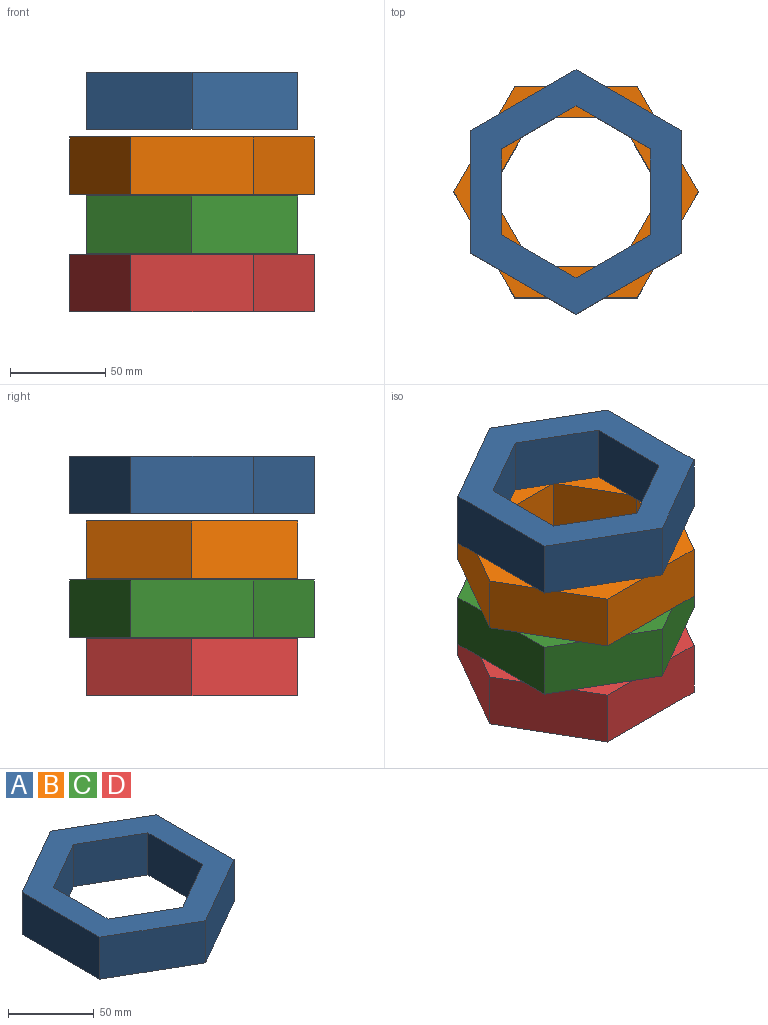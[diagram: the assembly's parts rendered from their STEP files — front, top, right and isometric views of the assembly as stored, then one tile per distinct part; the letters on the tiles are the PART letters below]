
ASSEMBLY  parts=4 mates=3
PART A: 14 faces, bbox 110.9x128x30 mm
  f0: plane 38.97x30mm, normal (0.5,-0.87,0), area 1350mm2, adj f1,f11,f12,f13
  f1: plane 38.97x30mm, normal (-0.5,-0.87,0), area 1350mm2, adj f0,f2,f12,f13
  f2: plane 45x30mm, normal (-1,0,0), area 1350mm2, adj f1,f3,f12,f13
  f3: plane 38.97x30mm, normal (-0.5,0.87,0), area 1350mm2, adj f2,f4,f12,f13
  f4: plane 38.97x30mm, normal (0.5,0.87,0), area 1350mm2, adj f3,f11,f12,f13
  f5: plane 64x30mm, normal (-1,0,0), area 1920mm2, adj f6,f10,f12,f13
  f6: plane 55.43x32mm, normal (-0.5,-0.87,0), area 1920mm2, adj f5,f7,f12,f13
  f7: plane 55.43x32mm, normal (0.5,-0.87,0), area 1920mm2, adj f6,f8,f12,f13
  f8: plane 64x30mm, normal (1,0,0), area 1920mm2, adj f7,f9,f12,f13
  f9: plane 55.43x32mm, normal (0.5,0.87,0), area 1920mm2, adj f8,f10,f12,f13
  f10: plane 55.43x32mm, normal (-0.5,0.87,0), area 1920mm2, adj f5,f9,f12,f13
  f11: plane 45x30mm, normal (1,0,0), area 1350mm2, adj f0,f4,f12,f13
  f12: plane 128x110.85mm, normal (0,0,1), area 5380.6mm2, adj f0,f1,f2,f3,f4,f5,f6,f7
  f13: plane 128x110.85mm, normal (0,0,-1), area 5380.6mm2, adj f0,f1,f2,f3,f4,f5,f6,f7
PART B: same geometry as A
PART C: same geometry as A
PART D: same geometry as A
PLACE A rot(axis=(0.49,0.76,-0.42),0deg) t=(75.23,11.66,-43.35)mm
PLACE B rot(axis=(0,0,1),90deg) t=(75.23,11.66,-77.31)mm
PLACE C t=(75.23,11.66,-108.22)mm
PLACE D rot(axis=(0,0,1),90deg) t=(75.23,11.66,-138.89)mm
MATE slider B.f13 <-> C.f12  axis (0,0,-1) through (75.23,11.66,-77.31)mm
MATE slider A.f13 <-> B.f13  axis (0,0,-1) through (75.23,11.66,-43.35)mm
MATE slider C.f13 <-> D.f13  axis (0,0,-1) through (75.23,11.66,-108.22)mm
